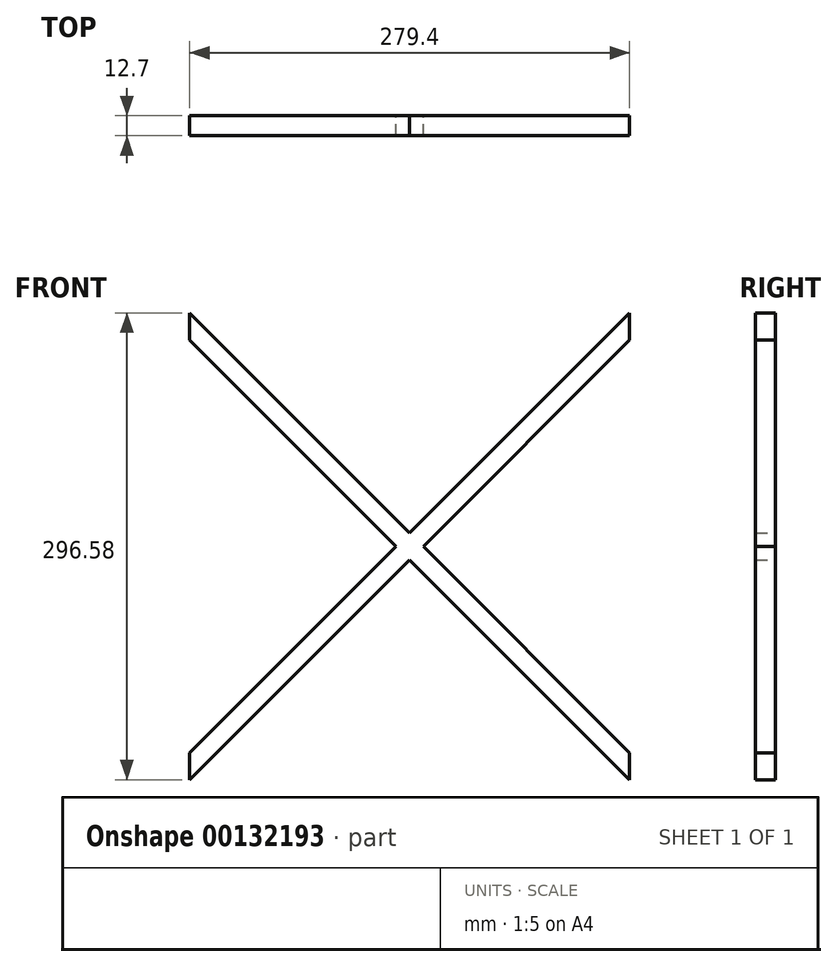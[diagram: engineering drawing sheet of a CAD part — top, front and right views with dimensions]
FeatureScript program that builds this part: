
annotation { "Feature Type Name" : "Feature", "Feature Type Description" : "" }
export const myFeature = defineFeature(function(context is Context, id is Id, definition is map)
    precondition{}
    {
        {
            var Q0;
            Q0=qCreatedBy(makeId("Front.planeOp"),FACE);
            var sketch = newSketch(context, id + "F0", { "sketchPlane" : qUnion([Q0])});
            skLineSegment(sketch, "E0.left", {"start": v(0, 0) * mm, "end": v(0, 8.59) * mm});
            skLineSegment(sketch, "E0.right", {"start": v(279.4, 0) * mm, "end": v(279.4, 8.59) * mm});
            skLineSegment(sketch, "E1", {"start": v(0, 279.4) * mm, "end": v(279.4, 0) * mm});
            skLineSegment(sketch, "E2", {"start": v(279.4, 279.4) * mm, "end": v(0, 0) * mm});
            skLineSegment(sketch, "E3", {"start": v(0, 270.81) * mm, "end": v(270.81, 0) * mm});
            skLineSegment(sketch, "E4", {"start": v(4.3, 283.7) * mm, "end": v(279.4, 8.59) * mm});
            skLineSegment(sketch, "E5", {"start": v(275.1, 283.7) * mm, "end": v(0, 8.59) * mm});
            skLineSegment(sketch, "E6", {"start": v(279.4, 270.81) * mm, "end": v(8.59, 0) * mm});
            skLineSegment(sketch, "E7", {"start": v(275.1, 283.7) * mm, "end": v(279.4, 287.99) * mm});
            skLineSegment(sketch, "E8", {"start": v(279.4, 279.4) * mm, "end": v(279.4, 287.99) * mm});
            skLineSegment(sketch, "E9", {"start": v(4.3, 283.7) * mm, "end": v(0, 287.99) * mm});
            skLineSegment(sketch, "E10", {"start": v(0, 279.4) * mm, "end": v(0, 287.99) * mm});
            skLineSegment(sketch, "E11", {"start": v(0, 0) * mm, "end": v(0, -8.59) * mm});
            skLineSegment(sketch, "E12", {"start": v(8.59, 0) * mm, "end": v(0, -8.59) * mm});
            skLineSegment(sketch, "E13", {"start": v(279.4, 0) * mm, "end": v(279.4, -8.59) * mm});
            skLineSegment(sketch, "E14", {"start": v(270.81, 0) * mm, "end": v(279.4, -8.59) * mm});
            skLineSegment(sketch, "E15.trimOffspring", {"start": v(0, 270.81) * mm, "end": v(0, 279.4) * mm});
            skLineSegment(sketch, "E16.trimOffspring", {"start": v(279.4, 270.81) * mm, "end": v(279.4, 279.4) * mm});
            skSolve(sketch);
        }
        {
            var Q0;
            Q0 = qSketchRegion(id + "F0", true);
            extrude(context, id + "F1", {"entities" : qUnion([Q0]), "depth" : 12.7 * mm});
        }
    });
